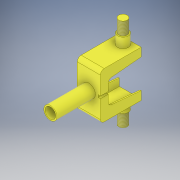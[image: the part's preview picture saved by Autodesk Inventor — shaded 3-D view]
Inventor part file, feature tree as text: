
AUTODESK INVENTOR PART (.ipt)
format: ipt  version: 2017 (Build 210142000, 142)  size: 210,432 bytes
history: native  units: in
note: dims shown in document units (in); Inventor stores cm internally (conversion verified against a paired STEP export)
features: sketch x4, extrude x3, shell x1, revolve x1, thread x1, mirror x1
ambient origin geometry x8: Origin, YZ Plane, XZ Plane, XY Plane, X Axis, Y Axis, Z Axis, Center Point
bodies: Solid1 (feature_tree)
feature tree (11):
  extrude  "Extrusion1"  Depth=2.0866in
  extrude  "Pin"  Depth=0.3937in
  extrude  "Extrusion4"  Depth=1.1811in
  shell  "Shell1"  Thickness=0.5906in
  revolve  "Revolution1"  [1 undecoded]
  thread  "Thread1"  [1 undecoded]
  mirror  "Mirror1"
  sketch  "Sketch1"  dims[d0=2.3622in d1=2.0866in]
  sketch  "Sketch2"  dims[d2=0.3937in d3=0.4331in]
  sketch  "Sketch3"  dims[d4=0.4331in d5=1.1811in d6=0.5906in]
  sketch  "Sketch5"  dims[d7=1.1811in d8=0.1969in d9=1.1811in d10=0.0in d11=0.1969in d12=0.6693in d13=1.9685in d14=0.0in d15=0.0625in d16=0.5118in d17=0.6693in d18=0.0591in d19=0.2165in d20=90.0deg d21=0.3937in d22=0.0in d28=0.1181in d29=0.1181in d30=0.0in d31=1.9685in d32=0.0in]
note: 2 required parameter values undecoded (feature->parameter linkage not recoverable at this tier; creation-order binding heuristic only, values carry confidence <= 0.55)